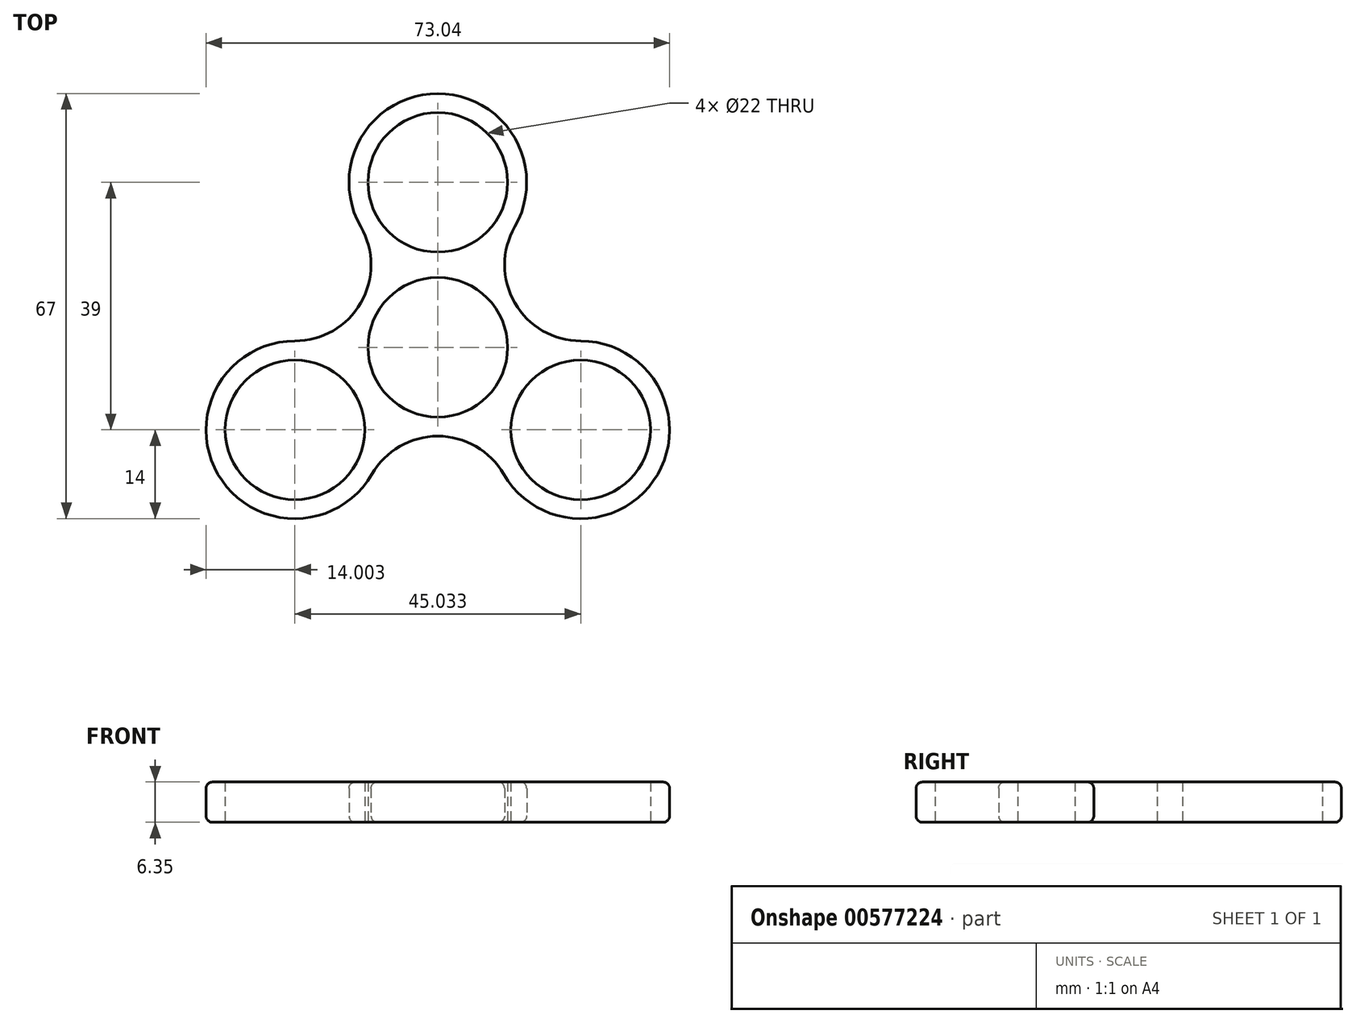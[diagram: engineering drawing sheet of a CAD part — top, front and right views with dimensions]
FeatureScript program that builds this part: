
annotation { "Feature Type Name" : "Feature", "Feature Type Description" : "" }
export const myFeature = defineFeature(function(context is Context, id is Id, definition is map)
    precondition{}
    {
        {
            var Q0;
            Q0=qCreatedBy(makeId("Top.planeOp"),FACE);
            var sketch = newSketch(context, id + "F0", { "sketchPlane" : qUnion([Q0])});
            skArc(sketch, "E0", {"start": v(12.12, 19) * mm, "mid": v(0, 40) * mm, "end": v(-12.12, 19) * mm});
            skArc(sketch, "E1", {"start": v(10.4, -20) * mm, "mid": v(34.64, -20) * mm, "end": v(22.52, 1) * mm});
            skArc(sketch, "E2", {"start": v(-22.52, 1) * mm, "mid": v(-34.64, -20) * mm, "end": v(-10.4, -20) * mm});
            skCircle(sketch, "E3", {"center": v(0, 0) * mm, "radius": 14 * mm});
            skArc(sketch, "E4", {"start": v(-22.52, 1) * mm, "mid": v(-12.12, 7) * mm, "end": v(-12.12, 19) * mm});
            skArc(sketch, "E5", {"start": v(12.12, 19) * mm, "mid": v(12.12, 7) * mm, "end": v(22.52, 1) * mm});
            skArc(sketch, "E6", {"start": v(10.4, -20) * mm, "mid": v(0, -14) * mm, "end": v(-10.4, -20) * mm});
            skCircle(sketch, "E7", {"center": v(-22.52, -13) * mm, "radius": 11 * mm});
            skCircle(sketch, "E8", {"center": v(22.52, -13) * mm, "radius": 11 * mm});
            skCircle(sketch, "E9", {"center": v(0, 26) * mm, "radius": 11 * mm});
            skCircle(sketch, "E10", {"center": v(0, 0) * mm, "radius": 11 * mm});
            skSolve(sketch);
        }
        {
            var Q0;
            Q0=qSketchRegion(id+"F0",true);
            extrude(context, id + "F1", {"entities" : qUnion([Q0]), "depth" : 6.35 * mm, "offsetDistance" : 25.4 * mm});
        }
        {
            var Q0;
            Q0=makeQuery(id+"F1.opExtrude","CAP_EDGE",EDGE,{"disambiguationData":[OSD([sQuery(id+"F0.wireOp",EDGE,"E6")])],"isStart":false});
            var Q1;
            Q1=makeQuery(id+"F1.opExtrude","CAP_EDGE",EDGE,{"disambiguationData":[OSD([sQuery(id+"F0.wireOp",EDGE,"E5")])],"isStart":false});
            var Q2;
            Q2=makeQuery(id+"F1.opExtrude","CAP_EDGE",EDGE,{"disambiguationData":[OSD([sQuery(id+"F0.wireOp",EDGE,"E6")])],"isStart":true});
            fillet(context, id + "F2", {"entities" : qUnion([Q0, Q1, Q2]), "radius" : 1 * mm, "tangentPropagation" : true, "allowEdgeOverflow" : false});
        }
    });
